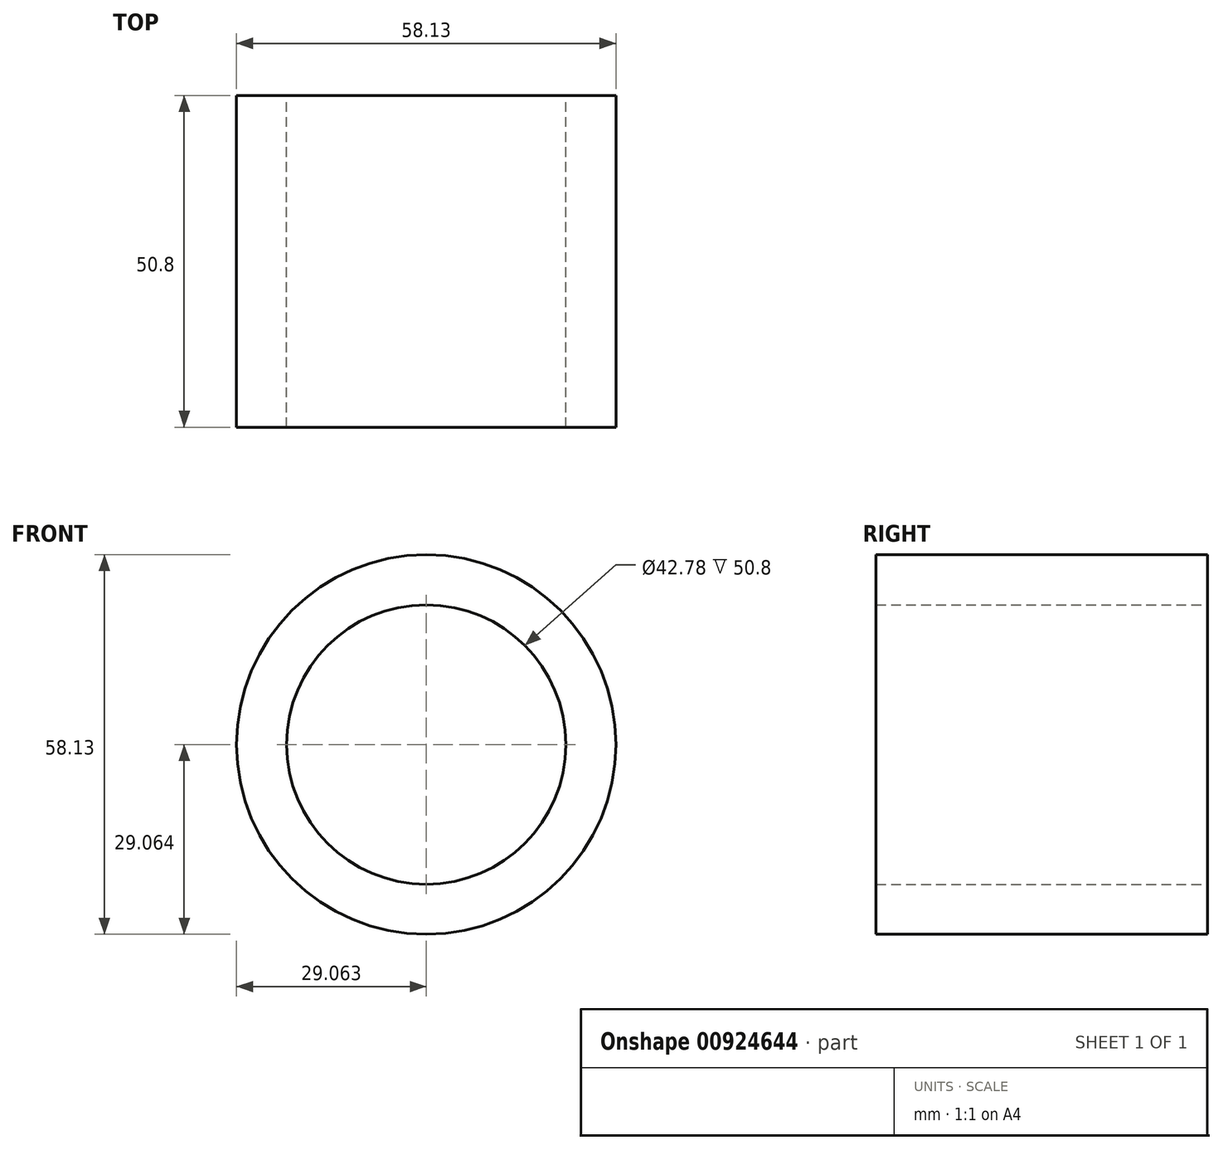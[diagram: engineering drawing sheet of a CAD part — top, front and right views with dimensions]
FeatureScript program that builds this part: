
annotation { "Feature Type Name" : "Feature", "Feature Type Description" : "" }
export const myFeature = defineFeature(function(context is Context, id is Id, definition is map)
    precondition{}
    {
        {
            var Q0;
            Q0=qCreatedBy(makeId("Front.planeOp"),FACE);
            var sketch = newSketch(context, id + "F0", { "sketchPlane" : qUnion([Q0])});
            skCircle(sketch, "E0", {"center": v(-40.99, -25.44) * mm, "radius": 21.4 * mm});
            skCircle(sketch, "E1", {"center": v(-40.99, -25.44) * mm, "radius": 29.06 * mm});
            skSolve(sketch);
        }
        {
            var Q0;
            Q0=makeQuery(id+"F0.imprint","IMPRINT",FACE,{"disambiguationData":[TD([[makeQuery(id+"F0.imprint","IMPRINT",EDGE,{"derivedFrom":sQuery(id+"F0.wireOp",EDGE,"E0")}),-1.0]])]});
            extrude(context, id + "F1", {"entities" : qUnion([Q0]), "depth" : 50.8 * mm, "offsetDistance" : 25.4 * mm});
        }
    });
